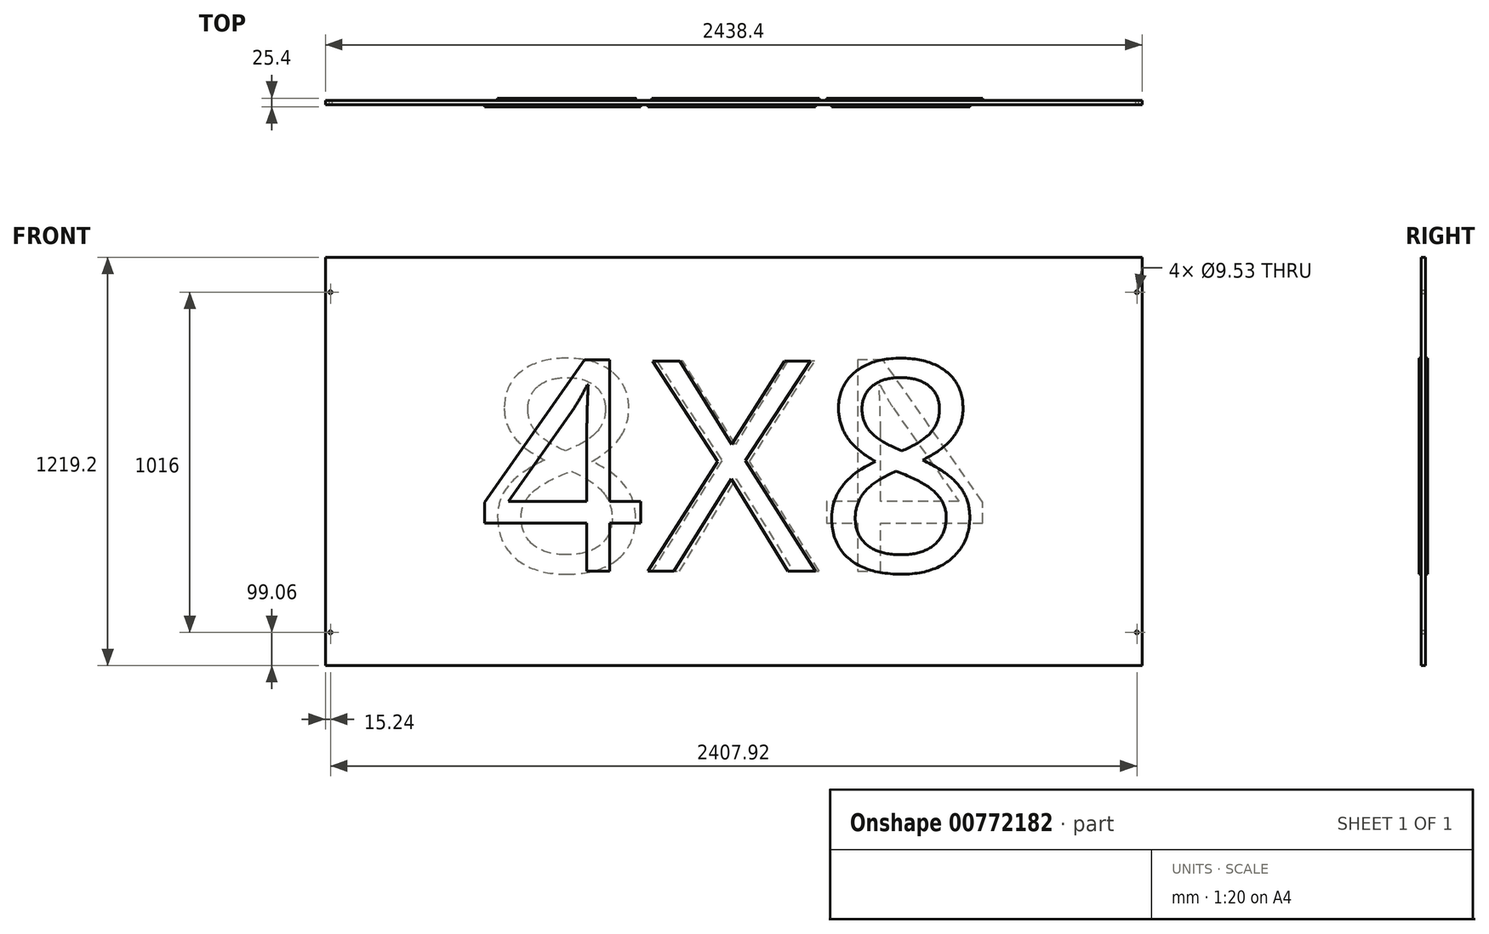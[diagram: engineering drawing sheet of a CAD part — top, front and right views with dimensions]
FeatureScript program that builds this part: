
annotation { "Feature Type Name" : "Feature", "Feature Type Description" : "" }
export const myFeature = defineFeature(function(context is Context, id is Id, definition is map)
    precondition{}
    {
        {
            var Q0;
            Q0=qCreatedBy(makeId("Front.planeOp"),FACE);
            var sketch = newSketch(context, id + "F0", { "sketchPlane" : qUnion([Q0])});
            skLineSegment(sketch, "E0.bottom", {"start": v(0, 0) * mm, "end": v(2438.4, 0) * mm});
            skLineSegment(sketch, "E0.top", {"start": v(0, 1219.2) * mm, "end": v(2438.4, 1219.2) * mm});
            skLineSegment(sketch, "E0.left", {"start": v(0, 0) * mm, "end": v(0, 1219.2) * mm});
            skLineSegment(sketch, "E0.right", {"start": v(2438.4, 0) * mm, "end": v(2438.4, 1219.2) * mm});
            skSolve(sketch);
        }
        {
            var Q0;
            Q0=makeQuery(id+"F0.imprint","IMPRINT",FACE,{"disambiguationData":[TD([[makeQuery(id+"F0.imprint","IMPRINT",EDGE,{"derivedFrom":sQuery(id+"F0.wireOp",EDGE,"E0.bottom")}),1.0]])]});
            extrude(context, id + "F1", {"entities" : qUnion([Q0]), "depth" : 12.7 * mm, "offsetDistance" : 25.4 * mm});
        }
        {
            var Q0;
            Q0=makeQuery(id+"F1.opExtrude","CAP_FACE",FACE,{"disambiguationData":[OSD([sQuery(id+"F0.wireOp",EDGE,"E0.bottom"),sQuery(id+"F0.wireOp",EDGE,"E0.top"),sQuery(id+"F0.wireOp",EDGE,"E0.left"),sQuery(id+"F0.wireOp",EDGE,"E0.right")])],"isStart":false});
            var sketch = newSketch(context, id + "F2", { "sketchPlane" : qUnion([Q0])});
            skCircle(sketch, "E1", {"center": v(15.24, 1115.06) * mm, "radius": 4.76 * mm});
            skCircle(sketch, "E2", {"center": v(15.24, 99.06) * mm, "radius": 4.76 * mm});
            skCircle(sketch, "E3", {"center": v(2423.16, 1115.06) * mm, "radius": 4.76 * mm});
            skCircle(sketch, "E4", {"center": v(2423.16, 99.06) * mm, "radius": 4.76 * mm});
            skSolve(sketch);
        }
        {
            var Q0;
            Q0=makeQuery(id+"F2.imprint","IMPRINT",FACE,{"disambiguationData":[TD([[makeQuery(id+"F2.imprint","IMPRINT",EDGE,{"derivedFrom":sQuery(id+"F2.wireOp",EDGE,"E3")}),1.0]])]});
            var Q1;
            Q1=makeQuery(id+"F2.imprint","IMPRINT",FACE,{"disambiguationData":[TD([[makeQuery(id+"F2.imprint","IMPRINT",EDGE,{"derivedFrom":sQuery(id+"F2.wireOp",EDGE,"E4")}),1.0]])]});
            var Q2;
            Q2=makeQuery(id+"F2.imprint","IMPRINT",FACE,{"disambiguationData":[TD([[makeQuery(id+"F2.imprint","IMPRINT",EDGE,{"derivedFrom":sQuery(id+"F2.wireOp",EDGE,"E2")}),1.0]])]});
            var Q3;
            Q3=makeQuery(id+"F2.imprint","IMPRINT",FACE,{"disambiguationData":[TD([[makeQuery(id+"F2.imprint","IMPRINT",EDGE,{"derivedFrom":sQuery(id+"F2.wireOp",EDGE,"E1")}),1.0]])]});
            extrude(context, id + "F3", {"entities" : qUnion([Q0, Q1, Q2, Q3]), "operationType" : NewBodyOperationType.REMOVE, "endBound" : BoundingType.THROUGH_ALL, "oppositeDirection" : true, "depth" : 25.4 * mm, "offsetDistance" : 25.4 * mm});
        }
        {
            var Q0;
            Q0=makeQuery(id+"F1.opExtrude","CAP_FACE",FACE,{"disambiguationData":[OSD([sQuery(id+"F0.wireOp",EDGE,"E0.bottom"),sQuery(id+"F0.wireOp",EDGE,"E0.top"),sQuery(id+"F0.wireOp",EDGE,"E0.left"),sQuery(id+"F0.wireOp",EDGE,"E0.right")])],"isStart":false});
            var sketch = newSketch(context, id + "F4", { "sketchPlane" : qUnion([Q0])});
            skText(sketch, "E5", { "text": "4X8", "fontName": "OpenSans-Regular.ttf"});
            const initialGuessF4  = {"E5": [0.4572, 0.2815, 1, 0, 0.6329]};
            skSetInitialGuess(sketch, initialGuessF4);
            skSolve(sketch);
        }
        {
            var Q0;
            Q0=makeQuery(id+"F4.imprint","IMPRINT",FACE,{"disambiguationData":[TD([[makeQuery(id+"F4.imprint","IMPRINT",EDGE,{"derivedFrom":sQuery(id+"F4.wireOp",EDGE,"E5.sketch_text.stroke-0")}),-1.0]])]});
            var Q1;
            Q1=makeQuery(id+"F4.imprint","IMPRINT",FACE,{"disambiguationData":[TD([[makeQuery(id+"F4.imprint","IMPRINT",EDGE,{"derivedFrom":sQuery(id+"F4.wireOp",EDGE,"E5.sketch_text.stroke-17")}),-1.0]])]});
            var Q2;
            Q2=makeQuery(id+"F4.imprint","IMPRINT",FACE,{"disambiguationData":[TD([[makeQuery(id+"F4.imprint","IMPRINT",EDGE,{"derivedFrom":sQuery(id+"F4.wireOp",EDGE,"E5.sketch_text.stroke-29")}),-1.0]])]});
            extrude(context, id + "F5", {"entities" : qUnion([Q0, Q1, Q2]), "operationType" : NewBodyOperationType.ADD, "depth" : 6.35 * mm, "offsetDistance" : 25.4 * mm});
        }
        {
            var Q0;
            Q0=makeQuery(id+"F1.opExtrude","CAP_FACE",FACE,{"disambiguationData":[OSD([sQuery(id+"F0.wireOp",EDGE,"E0.bottom"),sQuery(id+"F0.wireOp",EDGE,"E0.top"),sQuery(id+"F0.wireOp",EDGE,"E0.left"),sQuery(id+"F0.wireOp",EDGE,"E0.right")])],"isStart":true});
            var sketch = newSketch(context, id + "F6", { "sketchPlane" : qUnion([Q0])});
            skText(sketch, "E6", { "text": "4X8", "fontName": "OpenSans-Regular.ttf"});
            const initialGuessF6  = {"E6": [-1.9812, 0.2815, 1, 0, 0.6329]};
            skSetInitialGuess(sketch, initialGuessF6);
            skSolve(sketch);
        }
        {
            var Q0;
            Q0 = qSketchRegion(id + "F6", true);
            extrude(context, id + "F7", {"entities" : qUnion([Q0]), "operationType" : NewBodyOperationType.ADD, "depth" : 6.35 * mm, "offsetDistance" : 25.4 * mm});
        }
    });
